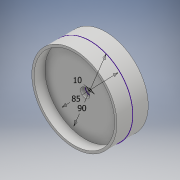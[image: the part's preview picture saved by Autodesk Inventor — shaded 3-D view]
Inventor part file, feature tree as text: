
AUTODESK INVENTOR PART (.ipt)
format: ipt  version: 2018 (Build 220112000, 112)  size: 116,736 bytes
history: native  units: mm
features: extrude x3, sketch x1
ambient origin geometry x8: Origin, YZ Plane, XZ Plane, XY Plane, X Axis, Y Axis, Z Axis, Center Point
bodies: Solid1 (feature_tree)
feature tree (4):
  sketch  "Sketch1"  dims[d0=85.0mm d1=10.0mm d2=0.0mm d3=90.0mm d4=33.0mm d5=0.0mm d6=10.0mm d7=33.0mm d8=0.0mm]
  extrude  "Extrusion1"  Depth=10.0mm TaperAngle=0.0deg
  extrude  "Extrusion2"  Depth=33.0mm
  extrude  "Extrusion3"  Depth=33.0mm TaperAngle=0.0deg
